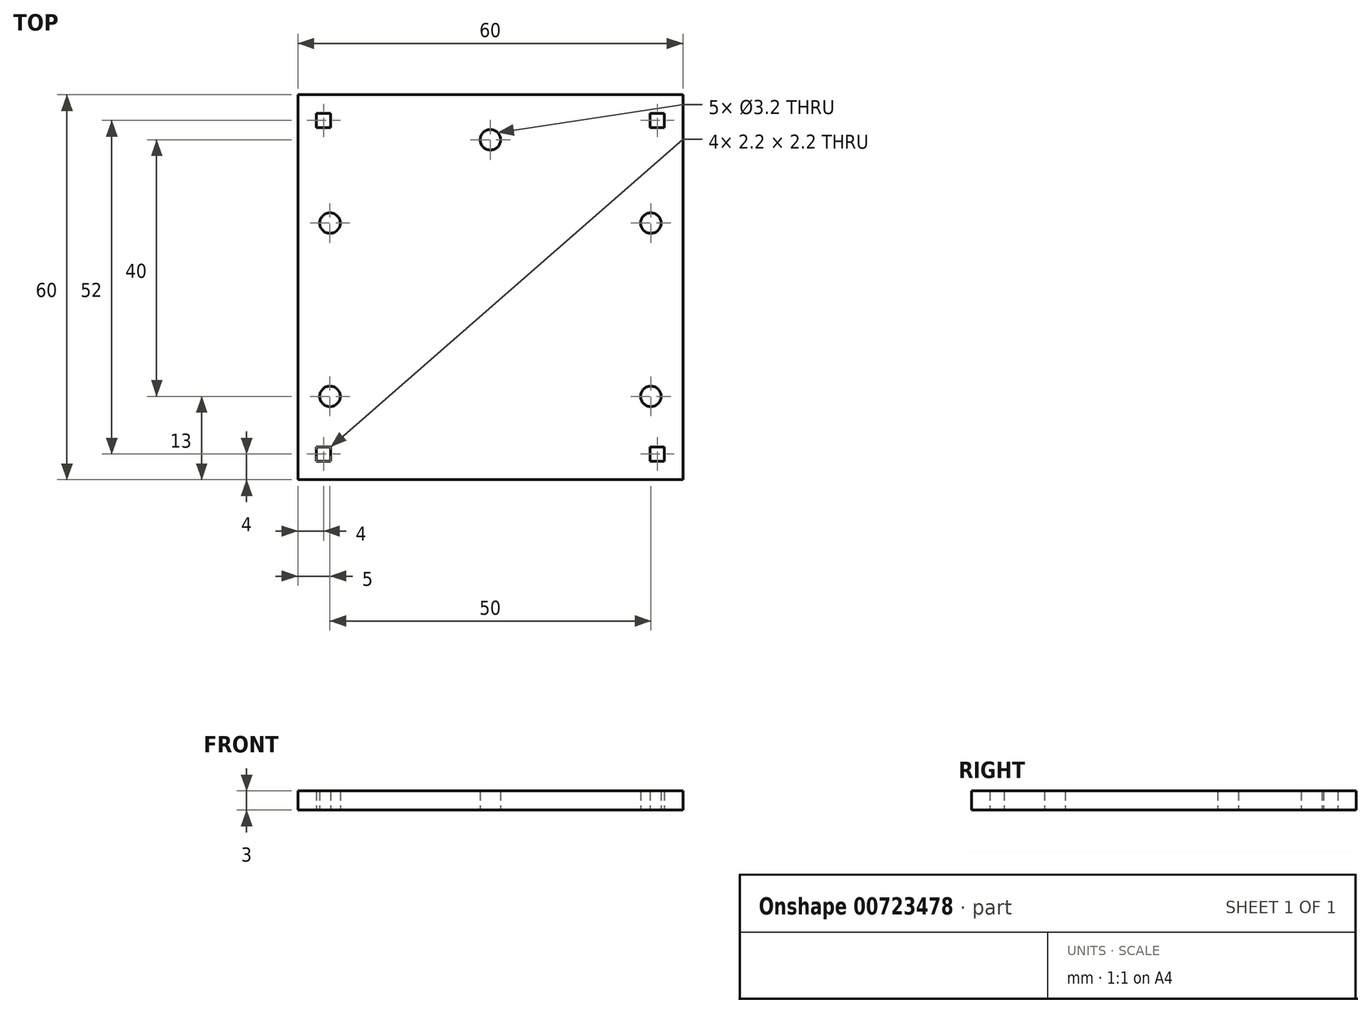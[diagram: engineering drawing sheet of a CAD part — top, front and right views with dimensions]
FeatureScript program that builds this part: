
annotation { "Feature Type Name" : "Feature", "Feature Type Description" : "" }
export const myFeature = defineFeature(function(context is Context, id is Id, definition is map)
    precondition{}
    {
        {
            var Q0;
            Q0=qCreatedBy(makeId("Top.planeOp"),FACE);
            var sketch = newSketch(context, id + "F0", { "sketchPlane" : qUnion([Q0])});
            skLineSegment(sketch, "E0.bottom", {"start": v(30, 30) * mm, "end": v(-30, 30) * mm});
            skLineSegment(sketch, "E0.top", {"start": v(30, -30) * mm, "end": v(-30, -30) * mm});
            skLineSegment(sketch, "E0.left", {"start": v(30, 30) * mm, "end": v(30, -30) * mm});
            skLineSegment(sketch, "E0.right", {"start": v(-30, 30) * mm, "end": v(-30, -30) * mm});
            skPoint(sketch, "E0.middle", {"position": v(0, 0) * mm});
            skSolve(sketch);
        }
        {
            var Q0;
            Q0 = qSketchRegion(id + "F0", true);
            extrude(context, id + "F1", {"entities" : qUnion([Q0]), "depth" : 3 * mm, "offsetDistance" : 25 * mm});
        }
        {
            var Q0;
            Q0=makeQuery(id+"F1.opExtrude","CAP_FACE",FACE,{"disambiguationData":[OSD([sQuery(id+"F0.wireOp",EDGE,"E0.bottom"),sQuery(id+"F0.wireOp",EDGE,"E0.top"),sQuery(id+"F0.wireOp",EDGE,"E0.left"),sQuery(id+"F0.wireOp",EDGE,"E0.right")])],"isStart":true});
            var sketch = newSketch(context, id + "F2", { "sketchPlane" : qUnion([Q0])});
            skCircle(sketch, "E1", {"center": v(-25, -10) * mm, "radius": 1.6 * mm});
            skCircle(sketch, "E2", {"center": v(-25, 17) * mm, "radius": 1.6 * mm});
            skCircle(sketch, "E3", {"center": v(25, 17) * mm, "radius": 1.6 * mm});
            skCircle(sketch, "E4", {"center": v(25, -10) * mm, "radius": 1.6 * mm});
            skCircle(sketch, "E5", {"center": v(0, -23) * mm, "radius": 1.6 * mm});
            skSolve(sketch);
        }
        {
            var Q0;
            Q0 = qSketchRegion(id + "F2", true);
            extrude(context, id + "F3", {"entities" : qUnion([Q0]), "operationType" : NewBodyOperationType.REMOVE, "endBound" : BoundingType.THROUGH_ALL, "oppositeDirection" : true, "depth" : 25 * mm, "offsetDistance" : 25 * mm});
        }
        {
            var Q0;
            Q0=makeQuery(id+"F1.opExtrude","CAP_FACE",FACE,{"disambiguationData":[OSD([sQuery(id+"F0.wireOp",EDGE,"E0.bottom"),sQuery(id+"F0.wireOp",EDGE,"E0.top"),sQuery(id+"F0.wireOp",EDGE,"E0.left"),sQuery(id+"F0.wireOp",EDGE,"E0.right")])],"isStart":true});
            var sketch = newSketch(context, id + "F4", { "sketchPlane" : qUnion([Q0])});
            skLineSegment(sketch, "E6.bottom", {"start": v(27.1, 24.9) * mm, "end": v(24.9, 24.9) * mm});
            skLineSegment(sketch, "E6.top", {"start": v(27.1, 27.1) * mm, "end": v(24.9, 27.1) * mm});
            skLineSegment(sketch, "E6.left", {"start": v(27.1, 24.9) * mm, "end": v(27.1, 27.1) * mm});
            skLineSegment(sketch, "E6.right", {"start": v(24.9, 24.9) * mm, "end": v(24.9, 27.1) * mm});
            skPoint(sketch, "E6.middle", {"position": v(26, 26) * mm});
            skLineSegment(sketch, "E7.bottom", {"start": v(27.1, -27.1) * mm, "end": v(24.9, -27.1) * mm});
            skLineSegment(sketch, "E7.top", {"start": v(27.1, -24.9) * mm, "end": v(24.9, -24.9) * mm});
            skLineSegment(sketch, "E7.left", {"start": v(27.1, -27.1) * mm, "end": v(27.1, -24.9) * mm});
            skLineSegment(sketch, "E7.right", {"start": v(24.9, -27.1) * mm, "end": v(24.9, -24.9) * mm});
            skPoint(sketch, "E7.middle", {"position": v(26, -26) * mm});
            skLineSegment(sketch, "E8.bottom", {"start": v(-24.9, 24.9) * mm, "end": v(-27.1, 24.9) * mm});
            skLineSegment(sketch, "E8.top", {"start": v(-24.9, 27.1) * mm, "end": v(-27.1, 27.1) * mm});
            skLineSegment(sketch, "E8.left", {"start": v(-24.9, 24.9) * mm, "end": v(-24.9, 27.1) * mm});
            skLineSegment(sketch, "E8.right", {"start": v(-27.1, 24.9) * mm, "end": v(-27.1, 27.1) * mm});
            skPoint(sketch, "E8.middle", {"position": v(-26, 26) * mm});
            skLineSegment(sketch, "E9.bottom", {"start": v(-24.9, -27.1) * mm, "end": v(-27.1, -27.1) * mm});
            skLineSegment(sketch, "E9.top", {"start": v(-24.9, -24.9) * mm, "end": v(-27.1, -24.9) * mm});
            skLineSegment(sketch, "E9.left", {"start": v(-24.9, -27.1) * mm, "end": v(-24.9, -24.9) * mm});
            skLineSegment(sketch, "E9.right", {"start": v(-27.1, -27.1) * mm, "end": v(-27.1, -24.9) * mm});
            skPoint(sketch, "E9.middle", {"position": v(-26, -26) * mm});
            skSolve(sketch);
        }
        {
            var Q0;
            Q0 = qSketchRegion(id + "F4", true);
            extrude(context, id + "F5", {"entities" : qUnion([Q0]), "operationType" : NewBodyOperationType.REMOVE, "endBound" : BoundingType.THROUGH_ALL, "oppositeDirection" : true, "depth" : 25 * mm, "offsetDistance" : 25 * mm});
        }
    });
